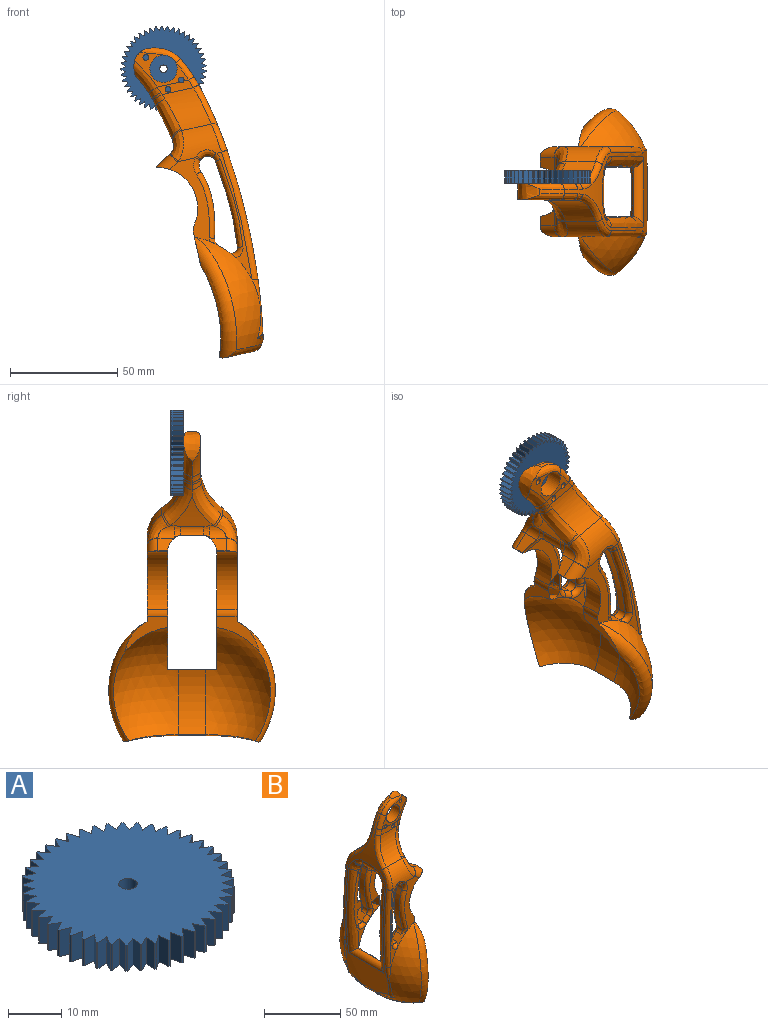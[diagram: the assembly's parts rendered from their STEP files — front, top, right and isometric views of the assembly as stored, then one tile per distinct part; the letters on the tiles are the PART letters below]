
ASSEMBLY  parts=2 mates=1
PART A: 138 faces, bbox 39.8x39.8x6 mm
  f0: plane 6.04x0.34mm, normal (-1,-0.07,0), area 2mm2, adj f1,f134,f135,f136
  f1: plane 6.04x2.3mm, normal (-0.37,-0.93,0), area 15mm2, adj f0,f2,f135,f136
  f2: plane 6.04x1.96mm, normal (-0.61,0.79,0), area 15mm2, adj f1,f3,f135,f136
  f3: plane 6.04x0.33mm, normal (-0.98,-0.21,0), area 2mm2, adj f2,f4,f135,f136
  f4: plane 6.04x2.41mm, normal (-0.23,-0.97,0), area 15mm2, adj f3,f5,f135,f136
  f5: plane 6.04x1.77mm, normal (-0.71,0.7,0), area 15mm2, adj f4,f6,f135,f136
  f6: plane 6.04x0.32mm, normal (-0.94,-0.34,0), area 2mm2, adj f5,f7,f135,f136
  f7: plane 6.04x2.47mm, normal (-0.1,-1,0), area 15mm2, adj f6,f8,f135,f136
  f8: plane 6.04x1.99mm, normal (-0.8,0.59,0), area 15mm2, adj f7,f9,f135,f136
  f9: plane 6.04x0.3mm, normal (-0.88,-0.47,0), area 2mm2, adj f8,f10,f135,f136
  f10: plane 6.04x2.47mm, normal (0.04,-1,0), area 15mm2, adj f9,f11,f135,f136
  f11: plane 6.04x2.18mm, normal (-0.88,0.48,0), area 15mm2, adj f10,f12,f135,f136
  f12: plane 6.04x0.27mm, normal (-0.81,-0.59,0), area 2mm2, adj f11,f13,f135,f136
  f13: plane 6.04x2.44mm, normal (0.18,-0.98,0), area 15mm2, adj f12,f14,f135,f136
  f14: plane 6.04x2.32mm, normal (-0.94,0.35,0), area 15mm2, adj f13,f15,f135,f136
  f15: plane 6.04x0.24mm, normal (-0.72,-0.69,0), area 2mm2, adj f14,f16,f135,f136
  f16: plane 6.04x2.35mm, normal (0.32,-0.95,0), area 15mm2, adj f15,f17,f135,f136
  f17: plane 6.04x2.42mm, normal (-0.98,0.22,0), area 15mm2, adj f16,f18,f135,f136
  f18: plane 6.04x0.27mm, normal (-0.62,-0.79,0), area 2mm2, adj f17,f19,f135,f136
  f19: plane 6.04x2.22mm, normal (0.45,-0.9,0), area 15mm2, adj f18,f20,f135,f136
  f20: plane 6.04x2.47mm, normal (-1,0.08,0), area 15mm2, adj f19,f21,f135,f136
  f21: plane 6.04x0.29mm, normal (-0.5,-0.87,0), area 2mm2, adj f20,f22,f135,f136
  f22: plane 6.04x2.04mm, normal (0.57,-0.82,0), area 15mm2, adj f21,f23,f135,f136
  f23: plane 6.04x2.47mm, normal (-1,-0.06,0), area 15mm2, adj f22,f24,f135,f136
  f24: plane 6.04x0.31mm, normal (-0.37,-0.93,0), area 2mm2, adj f23,f25,f135,f136
  f25: plane 6.04x1.83mm, normal (0.67,-0.74,0), area 15mm2, adj f24,f26,f135,f136
  f26: plane 6.04x2.43mm, normal (-0.98,-0.2,0), area 15mm2, adj f25,f27,f135,f136
  f27: plane 6.04x0.33mm, normal (-0.24,-0.97,0), area 2mm2, adj f26,f28,f135,f136
  f28: plane 6.04x1.91mm, normal (0.77,-0.64,0), area 15mm2, adj f27,f29,f135,f136
  f29: plane 6.04x2.33mm, normal (-0.94,-0.33,0), area 15mm2, adj f28,f30,f135,f136
  f30: plane 6.04x0.34mm, normal (-0.1,-0.99,0), area 2mm2, adj f29,f31,f135,f136
  f31: plane 6.04x2.11mm, normal (0.85,-0.52,0), area 15mm2, adj f30,f32,f135,f136
  f32: plane 6.04x2.2mm, normal (-0.89,-0.46,0), area 15mm2, adj f31,f33,f135,f136
  f33: plane 6.04x0.34mm, normal (0.03,-1,0), area 2mm2, adj f32,f34,f135,f136
  f34: plane 6.04x2.27mm, normal (0.92,-0.4,0), area 15mm2, adj f33,f35,f135,f136
  f35: plane 6.04x2.01mm, normal (-0.81,-0.58,0), area 15mm2, adj f34,f36,f135,f136
  f36: plane 6.04x0.33mm, normal (0.17,-0.98,0), area 2mm2, adj f35,f37,f135,f136
  f37: plane 6.04x2.39mm, normal (0.96,-0.27,0), area 15mm2, adj f36,f38,f135,f136
  f38: plane 6.04x1.79mm, normal (-0.72,-0.69,0), area 15mm2, adj f37,f39,f135,f136
  f39: plane 6.04x0.32mm, normal (0.31,-0.95,0), area 2mm2, adj f38,f40,f135,f136
  f40: plane 6.04x2.46mm, normal (0.99,-0.13,0), area 15mm2, adj f39,f41,f135,f136
  f41: plane 6.04x1.94mm, normal (-0.62,-0.78,0), area 15mm2, adj f40,f42,f135,f136
  f42: plane 6.04x0.3mm, normal (0.44,-0.9,0), area 2mm2, adj f41,f43,f135,f136
  f43: plane 6.04x2.48mm, normal (1,0.01,0), area 15mm2, adj f42,f44,f135,f136
  f44: plane 6.04x2.14mm, normal (-0.51,-0.86,0), area 15mm2, adj f43,f45,f135,f136
  f45: plane 6.04x0.28mm, normal (0.56,-0.83,0), area 2mm2, adj f44,f46,f135,f136
  f46: plane 6.04x2.45mm, normal (0.99,0.15,0), area 15mm2, adj f45,f47,f135,f136
  f47: plane 6.04x2.29mm, normal (-0.38,-0.92,0), area 15mm2, adj f46,f48,f135,f136
  f48: plane 6.04x0.25mm, normal (0.67,-0.74,0), area 2mm2, adj f47,f49,f135,f136
  f49: plane 6.04x2.38mm, normal (0.96,0.28,0), area 15mm2, adj f48,f50,f135,f136
  f50: plane 6.04x2.4mm, normal (-0.25,-0.97,0), area 15mm2, adj f49,f51,f135,f136
  f51: plane 6.04x0.26mm, normal (0.77,-0.64,0), area 2mm2, adj f50,f52,f135,f136
  f52: plane 6.04x2.25mm, normal (0.91,0.41,0), area 15mm2, adj f51,f53,f135,f136
  f53: plane 6.04x2.46mm, normal (-0.11,-0.99,0), area 15mm2, adj f52,f54,f135,f136
  f54: plane 6.04x0.29mm, normal (0.85,-0.53,0), area 2mm2, adj f53,f55,f135,f136
  f55: plane 6.04x2.09mm, normal (0.84,0.54,0), area 15mm2, adj f54,f56,f135,f136
  f56: plane 6.04x2.48mm, normal (0.03,-1,0), area 15mm2, adj f55,f57,f135,f136
  f57: plane 6.04x0.31mm, normal (0.91,-0.41,0), area 2mm2, adj f56,f58,f135,f136
  f58: plane 6.04x1.88mm, normal (0.76,0.65,0), area 15mm2, adj f57,f59,f135,f136
  f59: plane 6.04x2.44mm, normal (0.17,-0.99,0), area 15mm2, adj f58,f60,f135,f136
  f60: plane 6.04x0.32mm, normal (0.96,-0.28,0), area 2mm2, adj f59,f61,f135,f136
  f61: plane 6.04x1.85mm, normal (0.66,0.75,0), area 15mm2, adj f60,f62,f135,f136
  f62: plane 6.04x2.36mm, normal (0.3,-0.95,0), area 15mm2, adj f61,f63,f135,f136
  f63: plane 6.04x0.33mm, normal (0.99,-0.14,0), area 2mm2, adj f62,f64,f135,f136
  f64: plane 6.04x2.06mm, normal (0.55,0.83,0), area 15mm2, adj f63,f65,f135,f136
  f65: plane 6.04x2.23mm, normal (0.43,-0.9,0), area 15mm2, adj f64,f66,f135,f136
  f66: plane 6.04x0.34mm, normal (1,0,0), area 2mm2, adj f65,f67,f135,f136
  f67: plane 6.04x2.23mm, normal (0.43,0.9,0), area 15mm2, adj f66,f68,f135,f136
  f68: plane 6.04x2.06mm, normal (0.55,-0.83,0), area 15mm2, adj f67,f69,f135,f136
  f69: plane 6.04x0.33mm, normal (0.99,0.14,0), area 2mm2, adj f68,f70,f135,f136
  f70: plane 6.04x2.36mm, normal (0.3,0.95,0), area 15mm2, adj f69,f71,f135,f136
  f71: plane 6.04x1.85mm, normal (0.66,-0.75,0), area 15mm2, adj f70,f72,f135,f136
  f72: plane 6.04x0.32mm, normal (0.96,0.28,0), area 2mm2, adj f71,f73,f135,f136
  f73: plane 6.04x2.44mm, normal (0.17,0.99,0), area 15mm2, adj f72,f74,f135,f136
  f74: plane 6.04x1.88mm, normal (0.76,-0.65,0), area 15mm2, adj f73,f75,f135,f136
  f75: plane 6.04x0.31mm, normal (0.91,0.41,0), area 2mm2, adj f74,f76,f135,f136
  f76: plane 6.04x2.48mm, normal (0.03,1,0), area 15mm2, adj f75,f77,f135,f136
  f77: plane 6.04x2.09mm, normal (0.84,-0.54,0), area 15mm2, adj f76,f78,f135,f136
  f78: plane 6.04x0.29mm, normal (0.85,0.53,0), area 2mm2, adj f77,f79,f135,f136
  f79: plane 6.04x2.46mm, normal (-0.11,0.99,0), area 15mm2, adj f78,f80,f135,f136
  f80: plane 6.04x2.25mm, normal (0.91,-0.41,0), area 15mm2, adj f79,f81,f135,f136
  f81: plane 6.04x0.26mm, normal (0.77,0.64,0), area 2mm2, adj f80,f82,f135,f136
  f82: plane 6.04x2.4mm, normal (-0.25,0.97,0), area 15mm2, adj f81,f83,f135,f136
  f83: plane 6.04x2.38mm, normal (0.96,-0.28,0), area 15mm2, adj f82,f84,f135,f136
  f84: plane 6.04x0.25mm, normal (0.67,0.74,0), area 2mm2, adj f83,f85,f135,f136
  f85: plane 6.04x2.29mm, normal (-0.38,0.92,0), area 15mm2, adj f84,f86,f135,f136
  f86: plane 6.04x2.45mm, normal (0.99,-0.15,0), area 15mm2, adj f85,f87,f135,f136
  f87: plane 6.04x0.28mm, normal (0.56,0.83,0), area 2mm2, adj f86,f88,f135,f136
  f88: plane 6.04x2.14mm, normal (-0.51,0.86,0), area 15mm2, adj f87,f89,f135,f136
  f89: plane 6.04x2.48mm, normal (1,-0.01,0), area 15mm2, adj f88,f90,f135,f136
  f90: plane 6.04x0.3mm, normal (0.44,0.9,0), area 2mm2, adj f89,f91,f135,f136
  f91: plane 6.04x1.94mm, normal (-0.62,0.78,0), area 15mm2, adj f90,f92,f135,f136
  f92: plane 6.04x2.46mm, normal (0.99,0.13,0), area 15mm2, adj f91,f93,f135,f136
  f93: plane 6.04x0.32mm, normal (0.31,0.95,0), area 2mm2, adj f92,f94,f135,f136
  f94: plane 6.04x1.79mm, normal (-0.72,0.69,0), area 15mm2, adj f93,f95,f135,f136
  f95: plane 6.04x2.39mm, normal (0.96,0.27,0), area 15mm2, adj f94,f96,f135,f136
  f96: plane 6.04x0.33mm, normal (0.17,0.98,0), area 2mm2, adj f95,f97,f135,f136
  f97: plane 6.04x2.01mm, normal (-0.81,0.58,0), area 15mm2, adj f96,f98,f135,f136
  f98: plane 6.04x2.27mm, normal (0.92,0.4,0), area 15mm2, adj f97,f99,f135,f136
  f99: plane 6.04x0.34mm, normal (0.03,1,0), area 2mm2, adj f98,f100,f135,f136
  f100: plane 6.04x2.2mm, normal (-0.89,0.46,0), area 15mm2, adj f99,f101,f135,f136
  f101: plane 6.04x2.11mm, normal (0.85,0.52,0), area 15mm2, adj f100,f102,f135,f136
  f102: plane 6.04x0.34mm, normal (-0.1,0.99,0), area 2mm2, adj f101,f103,f135,f136
  f103: plane 6.04x2.33mm, normal (-0.94,0.33,0), area 15mm2, adj f102,f104,f135,f136
  f104: plane 6.04x1.91mm, normal (0.77,0.64,0), area 15mm2, adj f103,f105,f135,f136
  f105: plane 6.04x0.33mm, normal (-0.24,0.97,0), area 2mm2, adj f104,f106,f135,f136
  f106: plane 6.04x2.43mm, normal (-0.98,0.2,0), area 15mm2, adj f105,f107,f135,f136
  f107: plane 6.04x1.83mm, normal (0.67,0.74,0), area 15mm2, adj f106,f108,f135,f136
  f108: plane 6.04x0.31mm, normal (-0.37,0.93,0), area 2mm2, adj f107,f109,f135,f136
  f109: plane 6.04x2.47mm, normal (-1,0.06,0), area 15mm2, adj f108,f110,f135,f136
  f110: plane 6.04x2.04mm, normal (0.57,0.82,0), area 15mm2, adj f109,f111,f135,f136
  f111: plane 6.04x0.29mm, normal (-0.5,0.87,0), area 2mm2, adj f110,f112,f135,f136
  f112: plane 6.04x2.47mm, normal (-1,-0.08,0), area 15mm2, adj f111,f113,f135,f136
  f113: plane 6.04x2.22mm, normal (0.45,0.9,0), area 15mm2, adj f112,f114,f135,f136
  f114: plane 6.04x0.27mm, normal (-0.62,0.79,0), area 2mm2, adj f113,f115,f135,f136
  f115: plane 6.04x2.42mm, normal (-0.98,-0.22,0), area 15mm2, adj f114,f116,f135,f136
  f116: plane 6.04x2.35mm, normal (0.32,0.95,0), area 15mm2, adj f115,f117,f135,f136
  f117: plane 6.04x0.24mm, normal (-0.72,0.69,0), area 2mm2, adj f116,f118,f135,f136
  f118: plane 6.04x2.32mm, normal (-0.94,-0.35,0), area 15mm2, adj f117,f119,f135,f136
  f119: plane 6.04x2.44mm, normal (0.18,0.98,0), area 15mm2, adj f118,f120,f135,f136
  f120: plane 6.04x0.27mm, normal (-0.81,0.59,0), area 2mm2, adj f119,f121,f135,f136
  f121: plane 6.04x2.18mm, normal (-0.88,-0.48,0), area 15mm2, adj f120,f122,f135,f136
  f122: plane 6.04x2.47mm, normal (0.04,1,0), area 15mm2, adj f121,f123,f135,f136
  f123: plane 6.04x0.3mm, normal (-0.88,0.47,0), area 2mm2, adj f122,f124,f135,f136
  f124: plane 6.04x1.99mm, normal (-0.8,-0.59,0), area 15mm2, adj f123,f125,f135,f136
  f125: plane 6.04x2.47mm, normal (-0.1,1,0), area 15mm2, adj f124,f126,f135,f136
  f126: plane 6.04x0.32mm, normal (-0.94,0.34,0), area 2mm2, adj f125,f127,f135,f136
  f127: plane 6.04x1.77mm, normal (-0.71,-0.7,0), area 15mm2, adj f126,f128,f135,f136
  f128: plane 6.04x2.41mm, normal (-0.23,0.97,0), area 15mm2, adj f127,f129,f135,f136
  f129: plane 6.04x0.33mm, normal (-0.98,0.21,0), area 2mm2, adj f128,f130,f135,f136
  f130: plane 6.04x1.96mm, normal (-0.61,-0.79,0), area 15mm2, adj f129,f131,f135,f136
  f131: plane 6.04x2.3mm, normal (-0.37,0.93,0), area 15mm2, adj f130,f132,f135,f136
  f132: plane 6.04x0.34mm, normal (-1,0.07,0), area 2mm2, adj f131,f133,f135,f136
  f133: plane 6.04x2.15mm, normal (-0.49,-0.87,0), area 15mm2, adj f132,f134,f135,f136
  f134: plane 6.04x2.15mm, normal (-0.49,0.87,0), area 15mm2, adj f0,f133,f135,f136
  f135: plane 39.83x39.81mm, normal (0,0,1), area 1116mm2, adj f0,f1,f2,f3,f4,f5,f6,f7
  f136: plane 39.83x39.81mm, normal (0,0,-1), area 1116mm2, adj f0,f1,f2,f3,f4,f5,f6,f7
  f137: cylinder r=1.75mm len=6.04mm, axis (0,0,1), area 66.5mm2, adj f135,f136
PART B: 154 faces, bbox 43x83.3x161.9 mm
  f0: plane 39.44x13.89mm, normal (0,-1,0), area 236.8mm2, adj f1,f2,f3,f4,f5,f6,f7,f8
  f1: bspline ~36.28x5.92mm, area 126.1mm2, adj f0,f2,f12,f13
  f2: torus R=6.35mm, axis (0,-1,0), area 12.2mm2, adj f0,f1,f14,f15
  f3: sphere r=40mm, area 1032.4mm2, adj f0,f4,f5,f15,f16,f17,f18,f19
  f4: cylinder r=40mm len=9.53mm, axis (-0.89,0,-0.46), area 3.8mm2, adj f0,f3,f152
  f5: torus R=34.56mm, axis (-0.87,0.5,0), area 477.9mm2, adj f0,f3,f6,f20,f21
  f6: plane 19.98x17.02mm, normal (1,0,0), area 112.4mm2, adj f0,f5,f7,f21,f152
  f7: cylinder r=5.08mm len=9.53mm, axis (0,1,0), area 31.3mm2, adj f0,f6,f8,f152
  f8: cylinder r=19.05mm len=30.09mm, axis (0,1,0), area 358.1mm2, adj f0,f7,f9,f22,f23,f152
  f9: cylinder r=5.08mm len=10.17mm, axis (-0.87,0,0.49), area 58.5mm2, adj f0,f8,f10,f22,f24
  f10: torus R=10.16mm, axis (0,-1,0), area 2mm2, adj f0,f9,f25,f26
  f11: cylinder r=17.18mm len=20.7mm, axis (1,0,0), area 240.4mm2, adj f0,f16,f26,f27,f28,f29,f30
  f12: torus R=7.62mm, axis (0,-1,0), area 26.1mm2, adj f0,f1,f28,f31
  f13: extruded ~31.61x4.45mm, area 143mm2, adj f1,f14,f31,f32
  f14: cylinder r=3.81mm len=4.45mm, axis (0,-1,0), area 19mm2, adj f2,f13,f15,f33
  f15: cylinder r=37.24mm len=10.33mm, axis (0,-1,0), area 50.2mm2, adj f2,f3,f14,f34,f35,f36
  f16: plane 61.28x6.25mm, normal (0,-1,0), area 97mm2, adj f3,f11,f36,f37,f38,f39
  f17: bspline ~28.92x6.66mm, area 65mm2, adj f3,f18,f39,f40
  f18: bspline ~16.68x5.75mm, area 22.2mm2, adj f3,f17,f40
  f19: cylinder r=40mm len=12.7mm, axis (0,1,0), area 26.8mm2, adj f3,f40,f41,f42
  f20: torus R=29.73mm, axis (0,0,1), area 244.9mm2, adj f3,f5,f21,f42
  f21: sphere r=34.92mm, area 1737.2mm2, adj f5,f6,f20,f43,f44,f45,f152
  f22: plane 6.53x0.53mm, normal (1,0,0), area 2.5mm2, adj f8,f9,f23,f24
  f23: cylinder r=5.08mm len=28.73mm, axis (-1,0,0), area 89.2mm2, adj f8,f22,f24,f46,f47,f48,f49,f152
  f24: plane 7.94x7.88mm, normal (0.49,0,0.87), area 48.3mm2, adj f9,f22,f23,f25,f46,f50
  f25: cylinder r=5.08mm len=7.55mm, axis (0,-1,0), area 38mm2, adj f10,f24,f26,f51,f52,f53
  f26: bspline ~14.85x10.66mm, area 93.8mm2, adj f10,f11,f25,f53
  f27: bspline ~10.79x5.06mm, area 32.7mm2, adj f11,f28,f38,f54
  f28: bspline ~4.05x3.77mm, area 2.5mm2, adj f11,f12,f27,f31
  f29: cylinder r=25.4mm len=19.49mm, axis (1,0,0), area 319.2mm2, adj f11,f53,f55,f56,f57,f58
  f30: bspline ~15.42x9.9mm, area 63.7mm2, adj f11,f39,f40,f55
  f31: cylinder r=5.08mm len=5.52mm, axis (0,-1,0), area 26.9mm2, adj f12,f13,f28,f49,f54,f59
  f32: bspline ~36.28x5.93mm, area 126.1mm2, adj f13,f33,f59,f152
  f33: torus R=6.35mm, axis (0,-1,0), area 21.1mm2, adj f14,f32,f34,f152
  f34: torus R=34.7mm, axis (0,-1,0), area 21.5mm2, adj f15,f33,f60,f152
  f35: cylinder r=2.54mm len=4.45mm, axis (0,-1,0), area 26.1mm2, adj f15,f36,f60,f61,f62
  f36: torus R=5.08mm, axis (0,-1,0), area 24.2mm2, adj f15,f16,f35,f37
  f37: bspline ~49.48x5.46mm, area 166.3mm2, adj f16,f36,f38,f61
  f38: torus R=6.35mm, axis (0,-1,0), area 10.9mm2, adj f16,f27,f37,f54
  f39: bspline ~78.66x5.71mm, area 270.9mm2, adj f16,f17,f30,f40
  f40: extruded ~136.21x38.85mm, area 1334.2mm2, adj f17,f18,f19,f30,f39,f45,f47,f55
  f41: sphere r=40mm, area 1032.4mm2, adj f19,f63,f64,f81,f82,f83,f84,f85
  f42: cylinder r=5.08mm len=12.7mm, axis (0,-1,0), area 106mm2, adj f19,f20,f44,f84
  f43: plane 23.03x0.66mm, normal (0,0,1), area 7.6mm2, adj f21,f44,f45,f79,f80,f87
  f44: cylinder r=34.92mm len=29.42mm, axis (0,1,0), area 398.8mm2, adj f21,f42,f43,f87
  f45: bspline ~79.74x7.85mm, area 412mm2, adj f21,f40,f43,f47,f62,f80,f88,f89
  f46: plane 22.97x0.83mm, normal (0,0.71,-0.71), area 26.2mm2, adj f23,f24,f50,f73
  f47: bspline ~10.08x7.86mm, area 45.7mm2, adj f23,f40,f45,f73,f90
  f48: bspline ~10.77x3.7mm, area 25.5mm2, adj f23,f49,f54,f90
  f49: bspline ~4.44x3.76mm, area 4.6mm2, adj f23,f31,f48,f59
  f50: cylinder r=5.08mm len=21.37mm, axis (1,0,0), area 78.2mm2, adj f24,f46,f51,f74,f91
  f51: bspline ~5.31x2.81mm, area 14.2mm2, adj f25,f50,f52,f92
  f52: extruded ~20.13x15.16mm, area 123.5mm2, adj f25,f51,f58,f92,f93,f94,f95
  f53: bspline ~7.5x7.23mm, area 7.9mm2, adj f25,f26,f29,f58
  f54: cylinder r=3.81mm len=6.36mm, axis (0,-1,0), area 38.7mm2, adj f27,f31,f38,f48,f61,f88,f90
  f55: bspline ~24.47x13.55mm, area 95.9mm2, adj f29,f30,f40,f72
  f56: cylinder r=50.8mm len=16.38mm, axis (1,0,0), area 52.9mm2, adj f29,f72,f96,f97,f98,f99,f100
  f57: bspline ~6.11x5.76mm, area 18.2mm2, adj f29,f58,f99,f101
  f58: bspline ~22.01x16.05mm, area 166.1mm2, adj f29,f52,f53,f57,f95
  f59: torus R=7.62mm, axis (0,-1,0), area 22.8mm2, adj f31,f32,f49,f152
  f60: torus R=5.08mm, axis (0,-1,0), area 26.4mm2, adj f34,f35,f62,f152
  f61: extruded ~41.3x4.38mm, area 180.1mm2, adj f35,f37,f54,f89
  f62: bspline ~3.88x3.23mm, area 6.4mm2, adj f35,f45,f60,f89
  f63: bspline ~15.61x5.4mm, area 24mm2, adj f40,f41,f64
  f64: bspline ~31.5x7.94mm, area 65mm2, adj f40,f41,f63,f65
  f65: bspline ~78.66x5.71mm, area 270.9mm2, adj f40,f64,f66,f85
  f66: bspline ~15.42x9.9mm, area 63.7mm2, adj f40,f65,f67,f102
  f67: bspline ~25.76x15.33mm, area 95.9mm2, adj f40,f66,f68,f103
  f68: bspline ~10.99x6mm, area 18.7mm2, adj f40,f67,f69,f104
  f69: bspline ~32.08x18.71mm, area 45.2mm2, adj f40,f68,f105,f106
  f70: extruded ~9.97x7.4mm, area 25.9mm2, adj f40,f105,f107,f108
  f71: bspline ~32.08x18.71mm, area 45.2mm2, adj f40,f72,f97,f108
  f72: bspline ~10.99x6mm, area 18.7mm2, adj f40,f55,f56,f71
  f73: bspline ~9.95x9.58mm, area 10.2mm2, adj f40,f46,f47,f74
  f74: bspline ~9.09x7.82mm, area 46.5mm2, adj f40,f50,f73,f75
  f75: cylinder r=5.08mm len=11.03mm, axis (0,-1,0), area 97.1mm2, adj f40,f74,f76,f91
  f76: bspline ~9.09x7.82mm, area 46.4mm2, adj f40,f75,f77,f109
  f77: bspline ~9.95x9.58mm, area 10.2mm2, adj f40,f76,f78,f110
  f78: bspline ~10.51x7.44mm, area 45.6mm2, adj f40,f77,f79,f111,f112
  f79: bspline ~79.74x7.85mm, area 412mm2, adj f40,f43,f78,f80,f87,f113,f114,f115
  f80: cylinder r=3.81mm len=33.02mm, axis (0,-1,0), area 178.8mm2, adj f40,f43,f45,f79
  f81: cylinder r=40mm len=9.53mm, axis (-0.89,0,-0.46), area 3.8mm2, adj f41,f82,f153
  f82: plane 39.44x13.91mm, normal (0,1,0), area 236.8mm2, adj f41,f81,f83,f102,f116,f117,f118,f119
  f83: torus R=34.56mm, axis (-0.87,-0.5,0), area 477.9mm2, adj f41,f82,f84,f87,f116
  f84: torus R=29.73mm, axis (0,0,1), area 244.9mm2, adj f41,f42,f83,f87
  f85: plane 61.28x6.25mm, normal (0,1,0), area 97mm2, adj f41,f65,f102,f124,f125,f126
  f86: cylinder r=37.24mm len=10.33mm, axis (0,-1,0), area 50.2mm2, adj f41,f123,f125,f127,f128,f129
  f87: sphere r=34.92mm, area 1737.2mm2, adj f43,f44,f79,f83,f84,f116,f153
  f88: bspline ~4.15x3.54mm, area 9.3mm2, adj f45,f54,f89,f90
  f89: bspline ~45.74x6.38mm, area 216mm2, adj f45,f61,f62,f88
  f90: bspline ~3.49x3.24mm, area 1.4mm2, adj f47,f48,f54,f88
  f91: plane 18.27x11.03mm, normal (0,0,-1), area 201.6mm2, adj f50,f75,f92,f109
  f92: cylinder r=5.08mm len=11.03mm, axis (0,-1,0), area 48.1mm2, adj f51,f52,f91,f94
  f93: cylinder r=5.08mm len=7.55mm, axis (0,-1,0), area 38mm2, adj f52,f94,f120,f130,f131,f132
  f94: bspline ~5.55x4.19mm, area 14.2mm2, adj f52,f92,f93,f109
  f95: bspline ~24.1x17.42mm, area 166.1mm2, adj f52,f58,f101,f103,f132
  f96: cylinder r=1.33mm len=7.63mm, axis (0,1,0), area 63.9mm2, adj f56,f104
  f97: plane 22.7x17.59mm, normal (0,-1,0), area 101.8mm2, adj f56,f71,f100,f107,f108,f133,f134,f135
  f98: bspline ~7.37x6.9mm, area 20mm2, adj f56,f99,f133,f136
  f99: bspline ~5.76x5.41mm, area 8.3mm2, adj f56,f57,f98,f137
  f100: cylinder r=1.33mm len=7.62mm, axis (0,1,0), area 63.8mm2, adj f56,f97,f104,f106
  f101: bspline ~6.18x5.81mm, area 18.2mm2, adj f57,f95,f103,f137
  f102: cylinder r=17.18mm len=20.7mm, axis (1,0,0), area 240.4mm2, adj f66,f82,f85,f103,f131,f138,f139
  f103: cylinder r=25.4mm len=19.49mm, axis (1,0,0), area 319.2mm2, adj f67,f95,f101,f102,f104,f132
  f104: cylinder r=50.8mm len=16.38mm, axis (1,0,0), area 52.9mm2, adj f68,f96,f100,f103,f106,f136,f137
  f105: bspline ~29.15x17.18mm, area 67.7mm2, adj f69,f70,f106,f107,f134
  f106: plane 22.7x17.59mm, normal (0,1,0), area 101.8mm2, adj f69,f100,f104,f105,f107,f134,f135,f140
  f107: extruded ~12.21x11.87mm, area 104.3mm2, adj f70,f97,f105,f106,f108,f133,f140
  f108: bspline ~29.15x17.18mm, area 67.7mm2, adj f70,f71,f97,f107,f134
  f109: cylinder r=5.08mm len=21.37mm, axis (1,0,0), area 78.2mm2, adj f76,f91,f94,f110,f130
  f110: plane 22.97x0.83mm, normal (0,-0.71,-0.71), area 26.2mm2, adj f77,f109,f112,f130
  f111: bspline ~3.49x3.24mm, area 1.4mm2, adj f78,f114,f141,f142
  f112: cylinder r=5.08mm len=28.73mm, axis (-1,0,0), area 89.2mm2, adj f78,f110,f118,f130,f142,f143,f144,f153
  f113: bspline ~44.9x6.38mm, area 216mm2, adj f79,f114,f115,f145
  f114: bspline ~4.15x3.54mm, area 9.3mm2, adj f79,f111,f113,f141
  f115: bspline ~3.88x3.23mm, area 6.4mm2, adj f79,f113,f127,f146
  f116: plane 19.99x17.04mm, normal (1,0,0), area 112.4mm2, adj f82,f83,f87,f117,f153
  f117: cylinder r=5.08mm len=9.53mm, axis (0,1,0), area 31.3mm2, adj f82,f116,f118,f153
  f118: cylinder r=19.05mm len=30.09mm, axis (0,1,0), area 358.1mm2, adj f82,f112,f117,f119,f143,f153
  f119: cylinder r=5.08mm len=10.17mm, axis (0.87,0,-0.49), area 58.5mm2, adj f82,f118,f120,f130,f143
  f120: torus R=10.16mm, axis (0,-1,0), area 2mm2, adj f82,f93,f119,f131
  f121: torus R=7.62mm, axis (0,-1,0), area 26.1mm2, adj f82,f122,f138,f147
  f122: bspline ~36.28x5.93mm, area 126.1mm2, adj f82,f121,f123,f148
  f123: torus R=6.35mm, axis (0,-1,0), area 12.2mm2, adj f82,f86,f122,f129
  f124: torus R=6.35mm, axis (0,-1,0), area 10.9mm2, adj f85,f126,f139,f141
  f125: torus R=5.08mm, axis (0,-1,0), area 24.2mm2, adj f85,f86,f126,f127
  f126: bspline ~49.48x5.47mm, area 166.3mm2, adj f85,f124,f125,f145
  f127: cylinder r=2.54mm len=4.45mm, axis (0,-1,0), area 26.1mm2, adj f86,f115,f125,f145,f146
  f128: torus R=34.7mm, axis (0,-1,0), area 21.5mm2, adj f86,f146,f149,f153
  f129: cylinder r=3.81mm len=4.45mm, axis (0,-1,0), area 19mm2, adj f86,f123,f148,f149
  f130: plane 7.94x7.88mm, normal (0.49,0,0.87), area 48.3mm2, adj f93,f109,f110,f112,f119,f143
  f131: bspline ~15.31x11.18mm, area 93.8mm2, adj f93,f102,f120,f132
  f132: bspline ~7.5x7.23mm, area 7.9mm2, adj f93,f95,f103,f131
  f133: bspline ~22.22x15.41mm, area 84.3mm2, adj f97,f98,f107,f140
  f134: cylinder r=6.35mm len=12.7mm, axis (0,-1,0), area 304mm2, adj f97,f105,f106,f108
  f135: cylinder r=1.33mm len=7.62mm, axis (0,1,0), area 63.8mm2, adj f97,f106
  f136: bspline ~8.06x7.13mm, area 20mm2, adj f98,f104,f137,f140
  f137: bspline ~5.91x5.43mm, area 8.3mm2, adj f99,f101,f104,f136
  f138: bspline ~4.33x4.05mm, area 2.5mm2, adj f102,f121,f139,f147
  f139: bspline ~10.47x5.06mm, area 32.7mm2, adj f102,f124,f138,f141
  f140: bspline ~22.22x15.41mm, area 84.3mm2, adj f106,f107,f133,f136
  f141: cylinder r=3.81mm len=6.36mm, axis (0,-1,0), area 38.7mm2, adj f111,f114,f124,f139,f142,f145,f147
  f142: bspline ~10.88x3.7mm, area 25.5mm2, adj f111,f112,f141,f144
  f143: plane 6.53x0.53mm, normal (1,0,0), area 2.5mm2, adj f112,f118,f119,f130
  f144: bspline ~3.74x3.27mm, area 4.6mm2, adj f112,f142,f147,f150
  f145: extruded ~41.3x4.38mm, area 180.1mm2, adj f113,f126,f127,f141
  f146: torus R=5.08mm, axis (0,-1,0), area 26.4mm2, adj f115,f127,f128,f153
  f147: cylinder r=5.08mm len=5.52mm, axis (0,-1,0), area 26.9mm2, adj f121,f138,f141,f144,f148,f150
  f148: extruded ~31.61x4.45mm, area 143mm2, adj f122,f129,f147,f151
  f149: torus R=6.35mm, axis (0,-1,0), area 21.1mm2, adj f128,f129,f151,f153
  f150: torus R=7.62mm, axis (0,-1,0), area 22.8mm2, adj f144,f147,f151,f153
  f151: bspline ~36.28x5.92mm, area 126.1mm2, adj f148,f149,f150,f153
  f152: plane 61.87x29.06mm, normal (0,1,0), area 300.3mm2, adj f3,f4,f6,f7,f8,f21,f23,f32
  f153: plane 61.87x29.06mm, normal (0,-1,0), area 300.3mm2, adj f41,f79,f81,f87,f112,f116,f117,f118
PLACE A rot(axis=(0.99,-0.11,0.11),90.7deg) t=(26.53,34.13,92.37)mm
PLACE B rot(axis=(-0.11,0,0.99),180deg) t=(23.43,24.28,27.39)mm
MATE fastened A.f137 <-> B.f134  axis (0,-1,0) through (26.53,28.09,92.37)mm
